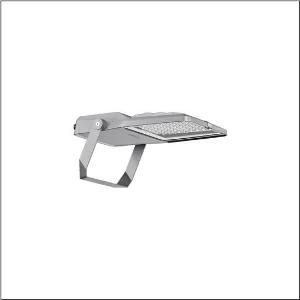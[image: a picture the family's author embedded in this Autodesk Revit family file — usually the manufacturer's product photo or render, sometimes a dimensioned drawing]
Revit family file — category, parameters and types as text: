
# Revit family: floodlight_fl_21_mini___pl33t_5xa7776b2f1a_8d7b
name_source: partatom
category: Lighting Fixtures
units: mm (PartAtom-declared; Revit-internal decimal feet)

## family parameters
Cut with Voids When Loaded = No
Host = Face
Light Source = No
Part Type = Normal
Room Calculation Point = No
Round Connector Dimension = Use Diameter
Shared = No

## types (1)
- --- (1 x LED, 6150 lm, 45.7 W, 3000K)
    Apparent Load = 46 VA
    CIE Flux Codes = 26 75 99 100 100
    Color Rendering = 70
    Color Temperature = 3000K
    Default Elevation = 1800 mm
    Description = Floodlight FL 21 mini, floodlight, primary light control with lens, of PMMA, primary optical cover: protective disc, of toughened safety glass, transparent, light distribution: PL33T, light emission: direct distribution, installation type: surface-mounted, LED, High Power LED, rated luminous flux: 6.150lm, luminous efficacy: 135lm/W, light colour: 730, colour temperature: 3000K, control: flexible luminous flux parameterisation, time-dependent luminous flux control, constant luminous flux control, overheat protection, presetting dimming logarithmic, with terminal, 6-pole, mains connection: 220..240V, AC, 50/60Hz, start of lifetime: 46W, end of service life: 48W, reduction: 22W, luminaire housing, of diecast aluminium, powder-coated, Siteco® metallic grey (DB 702S), corrosivity category C5 mid according to DIN EN ISO 12944, sealing non-destructively replaceable, mounting bracket, of steel, galvanised, powder-coated, Siteco® metallic grey (DB 702S), Smart Interface below and above, protection rating (complete): IP66, insulation class (complete): insulation class II (safety insulation), certification: CE, ENEC, VDE, protection symbol: D, impact resistance: IK08, permissible operating ambient temperature: -40..+40°C, permissible operating ambient temperature for outdoor applications: -40..+50°C, standard: DIN EN 12944, LABS conformity tested according to VDMA 24364:2018-05, packaging unit: 1 piece

Light Distribution: PL33T
    Height = 70 mm
    Lamp = 1 x LED
    Lamp Light Flux = 6150 lm
    Lamp Power = 45.7 W
    Lamp count = 1
    Length = 485 mm
    Luminous efficacy = 135 lm/W
    Manufacturer = Siteco
    ModVariant = No
    Model = 5XA7776B2F1A
    Number of Poles = 1
    OnlyDefault = Yes
    Power Factor = 1
    Product Name = Floodlight FL 21 mini | PL33T
    Product group = floodlight | pylon annexe
    ProductGroupID = 6200
    Protection Class = Protection class II
    Protection Degree = IP 66
    RLX_Detail_Level = 1
    RLX_Emergency_Light_Flux = 0 lm
    RLX_Emergency_Type = 0
    RLX_Emergency_Type_DB = No
    RlxData = <blob elided: 95829 chars, md5=b12031ed>
    Socket = socket
    Standby Power = 0 W
    System Light Flux = 6150 lm
    System Power = 46 W
    Type Comments = factory setting: luminous flux: 100 % | dim-lin: 254 | 463 mA
    Type Image = l_1006845.jpg
    URL = http://relux.com
    VarID = @adj_098797
    Voltage = 0 V
    Weight = 0.00 kg
    Width = 337 mm

## geometry (parser evidence)
native form markers: Blend x4, Sweep x11
no freeform markers — native parametric forms only
